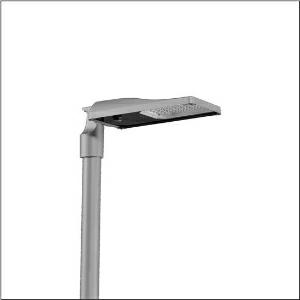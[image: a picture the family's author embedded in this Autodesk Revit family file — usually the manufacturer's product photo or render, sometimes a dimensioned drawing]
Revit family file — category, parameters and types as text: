
# Revit family: streetlight_sl_31_mini___st1_0a_5xh2d31r08ha_940f
name_source: partatom
category: Lighting Fixtures
units: mm (PartAtom-declared; Revit-internal decimal feet)

## family parameters
Cut with Voids When Loaded = No
Host = Face
Light Source = No
Part Type = Normal
Room Calculation Point = No
Round Connector Dimension = Use Diameter
Shared = No

## types (1)
- --- (1 x LED, 9230 lm, 68.3 W, 3000K)
    Apparent Load = 68 VA
    CIE Flux Codes = 37 72 97 100 100
    Color Rendering = 70
    Color Temperature = 3000K
    Default Elevation = 1800 mm
    Description = Streetlight SL 31 mini D4i, Desk-Remote mast luminaire for post-top, side-entry; light control with lens of PMMA; light distribution: ST1.0a, direct asymmetric distribution, for standard-compliant lighting for roads and squares; LED: luminous flux: 9.230lm, light colour: 730, colour temperature: 3000K; luminous efficacy: 135,1lm/W; control: pre-setting: logarithmic dimming characteristic, flexible luminous flux parameterisation, time-dependent luminous flux control, constant luminous flux control, power reduction, intelligent temperature release in ECG and LED module, overheat protection; luminaire housing, of diecast aluminium, SITECO metallic grey (DB 702S), corrosivity category C5 high according to DIN EN ISO 12944; cover of toughened safety glass, transparent, mast flange of diecast aluminium, SITECO metallic grey (DB 702S), spigot size: 76/60mm, mast flange included unmounted; with cable H07RN-F 2x 1.5mm², cable length: 8,5m, connection cable pre-assembled; mains connection: 220..240V, AC, 50/60Hz; power consumption (at start of service life): 68,3W / (at end of service life): 74,5W / (with reduced operation 50%): 29,5W; protection rating (complete): IP66; insulation class (complete): insulation class II (safety insulation); impact resistance: IK09; certification: CE, ENEC, ENEC+, VDE, UKCA, ZD4i; permissible operating ambient temperature for outdoor applications: -40..+50°C; packaging unit: 1 piece

Light Distribution: ST1.0a
    Height = 76 mm
    Lamp = 1 x LED
    Lamp Light Flux = 9230 lm
    Lamp Power = 68.3 W
    Lamp count = 1
    Length = 547 mm
    Luminous efficacy = 135 lm/W
    Manufacturer = Siteco
    ModVariant = No
    Model = 5XH2D31R08HA
    Number of Poles = 1
    OnlyDefault = Yes
    Power Factor = 1
    Product Name = Streetlight SL 31 mini | ST1.0a
    Product group = mast luminaire | pylon top
    ProductGroupID = 6100
    Protection Class = Protection class II
    Protection Degree = IP 66
    RLX_Detail_Level = 1
    RLX_Emergency_Light_Flux = 0 lm
    RLX_Emergency_Type = 0
    RLX_Emergency_Type_DB = No
    RlxData = <blob elided: 39345 chars, md5=a715c260>
    Socket = socket
    Standby Power = 0 W
    System Light Flux = 9230 lm
    System Power = 68 W
    Type Comments = factory setting: luminous flux: 100 % | dim-lin: 254 | 692 mA
    Type Image = l_1300328.jpg
    URL = http://relux.com
    VarID = @adj_020739
    Voltage = 0 V
    Weight = 0.00 kg
    Width = 265 mm

## geometry (parser evidence)
native form markers: Blend x4, Sweep x9
no freeform markers — native parametric forms only
